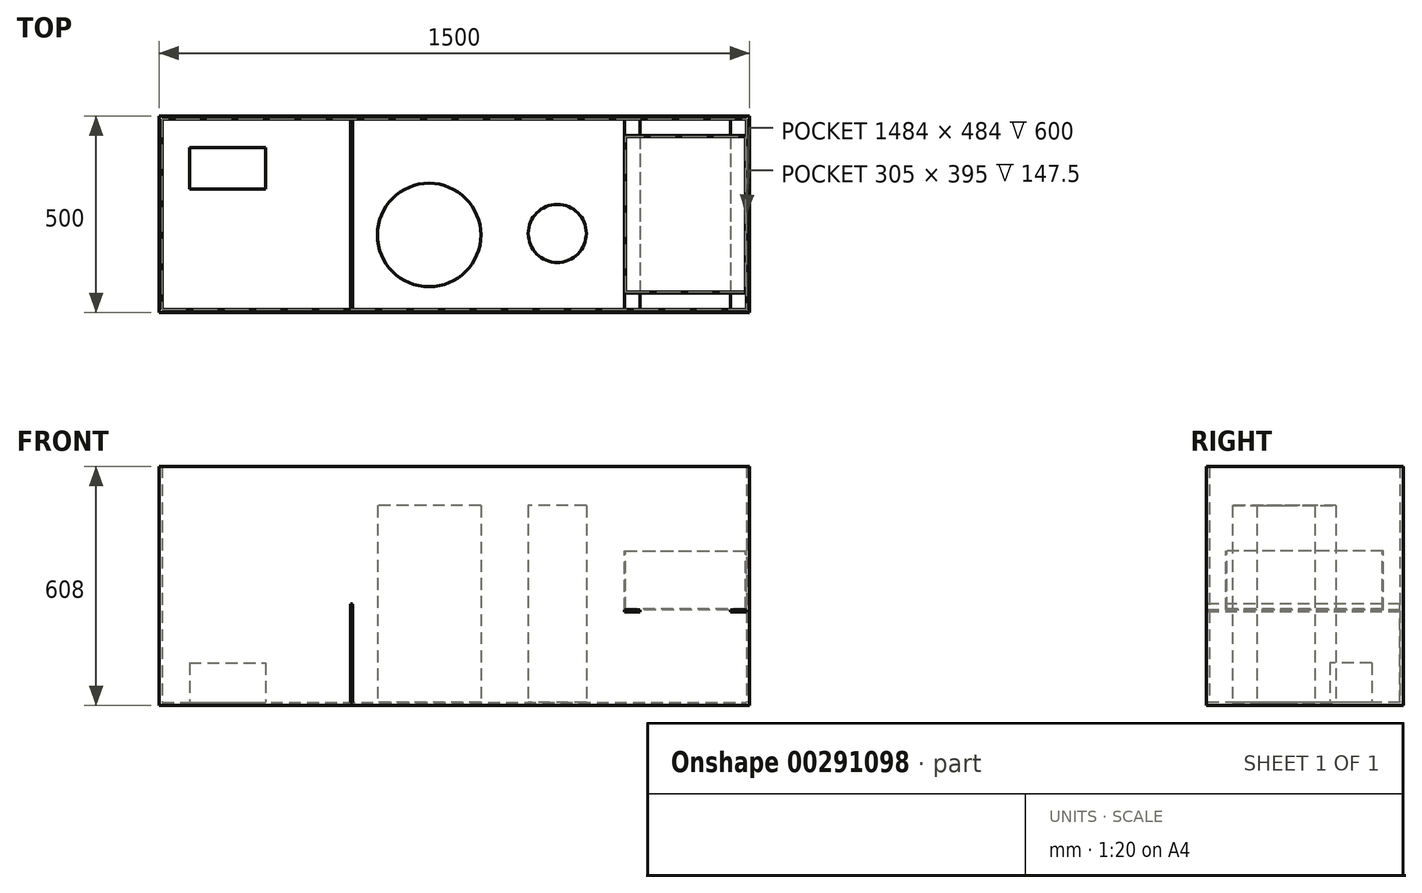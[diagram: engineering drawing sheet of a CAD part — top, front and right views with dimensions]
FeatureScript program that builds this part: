
annotation { "Feature Type Name" : "Feature", "Feature Type Description" : "" }
export const myFeature = defineFeature(function(context is Context, id is Id, definition is map)
    precondition{}
    {
        {
            var Q0;
            Q0=qCreatedBy(makeId("Top.planeOp"),FACE);
            var sketch = newSketch(context, id + "F0", { "sketchPlane" : qUnion([Q0])});
            skLineSegment(sketch, "E0.bottom", {"start": v(-750, 250) * mm, "end": v(750, 250) * mm});
            skLineSegment(sketch, "E0.top", {"start": v(-750, -250) * mm, "end": v(750, -250) * mm});
            skLineSegment(sketch, "E0.left", {"start": v(-750, 250) * mm, "end": v(-750, -250) * mm});
            skLineSegment(sketch, "E0.right", {"start": v(750, 250) * mm, "end": v(750, -250) * mm});
            skPoint(sketch, "E0.middle", {"position": v(0, 0) * mm});
            skLineSegment(sketch, "E1.bottom", {"start": v(-742, 242) * mm, "end": v(742, 242) * mm});
            skLineSegment(sketch, "E1.top", {"start": v(-742, -242) * mm, "end": v(742, -242) * mm});
            skLineSegment(sketch, "E1.left", {"start": v(-742, 242) * mm, "end": v(-742, -242) * mm});
            skLineSegment(sketch, "E1.right", {"start": v(742, 242) * mm, "end": v(742, -242) * mm});
            skSolve(sketch);
        }
        {
            var Q0;
            Q0=qSketchRegion(id+"F0",true);
            var Q1;
            Q1=makeQuery(id+"F0.imprint","IMPRINT",FACE,{"disambiguationData":[TD([[makeQuery(id+"F0.imprint","IMPRINT",EDGE,{"derivedFrom":sQuery(id+"F0.wireOp",EDGE,"E1.bottom")}),-1.0]])]});
            extrude(context, id + "F1", {"entities" : qUnion([Q0, Q1]), "oppositeDirection" : true, "depth" : 8 * mm});
        }
        {
            var Q0;
            Q0=qSketchRegion(id+"F0",true);
            extrude(context, id + "F2", {"entities" : qUnion([Q0]), "depth" : 600 * mm});
        }
        {
            var Q0;
            Q0=makeQuery(id+"F1.opExtrude","SWEPT_BODY",BODY,{"disambiguationData":[OSD([sQuery(id+"F0.wireOp",EDGE,"E0.bottom"),sQuery(id+"F0.wireOp",EDGE,"E0.top"),sQuery(id+"F0.wireOp",EDGE,"E0.left"),sQuery(id+"F0.wireOp",EDGE,"E0.right")])]});
            var Q1;
            Q1=makeQuery(id+"F2.opExtrude","SWEPT_BODY",BODY,{"disambiguationData":[OSD([sQuery(id+"F0.wireOp",EDGE,"E0.bottom"),sQuery(id+"F0.wireOp",EDGE,"E0.top"),sQuery(id+"F0.wireOp",EDGE,"E0.left"),sQuery(id+"F0.wireOp",EDGE,"E0.right"),sQuery(id+"F0.wireOp",EDGE,"E1.bottom"),sQuery(id+"F0.wireOp",EDGE,"E1.top"),sQuery(id+"F0.wireOp",EDGE,"E1.left"),sQuery(id+"F0.wireOp",EDGE,"E1.right")])]});
            booleanBodies(context, id + "F3", {"operationType" : BooleanOperationType.UNION, "tools" : qUnion([Q0, Q1])});
        }
        {
            var Q0;
            {var subQ0=sQuery(id+"F0.wireOp",EDGE,"E0.top");Q0=makeQuery(id+"F3.opBoolean","MERGE",FACE,{"derivedFrom":[makeQuery(id+"F1.opExtrude","SWEPT_FACE",FACE,{"disambiguationData":[OSD([subQ0])]}),makeQuery(id+"F2.opExtrude","SWEPT_FACE",FACE,{"disambiguationData":[OSD([subQ0])]})]});}
            var sketch = newSketch(context, id + "F4", { "sketchPlane" : qUnion([Q0])});
            skLineSegment(sketch, "E2", {"start": v(0, 0) * mm, "end": v(0, 341.46) * mm, "construction": true});
            skLineSegment(sketch, "E3.bottom", {"start": v(-258, 0) * mm, "end": v(-263, 0) * mm});
            skLineSegment(sketch, "E3.top", {"start": v(-258, 250) * mm, "end": v(-263, 250) * mm});
            skLineSegment(sketch, "E3.left", {"start": v(-258, 0) * mm, "end": v(-258, 250) * mm});
            skLineSegment(sketch, "E3.right", {"start": v(-263, 0) * mm, "end": v(-263, 250) * mm});
            skLineSegment(sketch, "E4.bottom", {"start": v(742, 230) * mm, "end": v(702, 230) * mm});
            skLineSegment(sketch, "E4.top", {"start": v(742, 235) * mm, "end": v(702, 235) * mm});
            skLineSegment(sketch, "E4.left", {"start": v(742, 230) * mm, "end": v(742, 235) * mm});
            skLineSegment(sketch, "E4.right", {"start": v(432, 230) * mm, "end": v(432, 235) * mm});
            skLineSegment(sketch, "E5", {"start": v(472, 235) * mm, "end": v(472, 230) * mm});
            skLineSegment(sketch, "E6", {"start": v(702, 235) * mm, "end": v(702, 230) * mm});
            skLineSegment(sketch, "E7", {"start": v(742, 235) * mm, "end": v(742, 214.93) * mm, "construction": true});
            skLineSegment(sketch, "E8.trimOffspring", {"start": v(472, 235) * mm, "end": v(432, 235) * mm});
            skLineSegment(sketch, "E9.trimOffspring", {"start": v(472, 230) * mm, "end": v(432, 230) * mm});
            skSolve(sketch);
        }
        {
            var Q0;
            Q0=qSketchRegion(id+"F4",true);
            var Q1;
            Q1=makeQuery(id+"F2.opExtrude","SWEPT_FACE",FACE,{"disambiguationData":[OSD([sQuery(id+"F0.wireOp",EDGE,"E1.bottom")])]});
            extrude(context, id + "F5", {"entities" : qUnion([Q0]), "endBound" : BoundingType.UP_TO_SURFACE, "oppositeDirection" : true, "endBoundEntityFace" : qUnion([Q1]), "depth" : 25 * mm});
        }
        {
            var Q0;
            Q0=qCreatedBy(makeId("Front.planeOp"),FACE);
            var sketch = newSketch(context, id + "F6", { "sketchPlane" : qUnion([Q0])});
            skLineSegment(sketch, "E10.0", {"start": v(472, 235) * mm, "end": v(432, 235) * mm});
            skLineSegment(sketch, "E11.0", {"start": v(742, 235) * mm, "end": v(702, 235) * mm});
            skLineSegment(sketch, "E12.bottom", {"start": v(432, 235) * mm, "end": v(742, 235) * mm});
            skLineSegment(sketch, "E12.top", {"start": v(432, 385) * mm, "end": v(742, 385) * mm});
            skLineSegment(sketch, "E12.left", {"start": v(432, 235) * mm, "end": v(432, 385) * mm});
            skLineSegment(sketch, "E12.right", {"start": v(742, 235) * mm, "end": v(742, 385) * mm});
            skSolve(sketch);
        }
        {
            var Q0;
            Q0 = qSketchRegion(id + "F6", true);
            extrude(context, id + "F7", {"entities" : qUnion([Q0]), "oppositeDirection" : true, "depth" : 200 * mm, "hasSecondDirection" : true, "secondDirectionOppositeDirection" : false, "secondDirectionDepth" : 200 * mm});
        }
        {
            var Q0;
            Q0=makeQuery(id+"F7.opExtrude","SWEPT_FACE",FACE,{"disambiguationData":[OSD([sQuery(id+"F6.wireOp",EDGE,"E12.top")])]});
            shell(context, id + "F8", {"entities" : qUnion([Q0]), "thickness" : 2.5 * mm});
        }
        {
            var Q0;
            Q0=makeQuery(id+"F1.opExtrude","CAP_FACE",FACE,{"disambiguationData":[OSD([sQuery(id+"F0.wireOp",EDGE,"E0.bottom"),sQuery(id+"F0.wireOp",EDGE,"E0.top"),sQuery(id+"F0.wireOp",EDGE,"E0.left"),sQuery(id+"F0.wireOp",EDGE,"E0.right")])],"isStart":true});
            var sketch = newSketch(context, id + "F9", { "sketchPlane" : qUnion([Q0])});
            skCircle(sketch, "E13", {"center": v(-64.04, -52.45) * mm, "radius": 131.48 * mm});
            skCircle(sketch, "E14", {"center": v(261.6, -48.37) * mm, "radius": 73.85 * mm});
            skSolve(sketch);
        }
        {
            var Q0;
            Q0 = qSketchRegion(id + "F9", true);
            extrude(context, id + "F10", {"entities" : qUnion([Q0]), "depth" : 500 * mm});
        }
        {
            var Q0;
            Q0=makeQuery(id+"F1.opExtrude","CAP_FACE",FACE,{"disambiguationData":[OSD([sQuery(id+"F0.wireOp",EDGE,"E0.bottom"),sQuery(id+"F0.wireOp",EDGE,"E0.top"),sQuery(id+"F0.wireOp",EDGE,"E0.left"),sQuery(id+"F0.wireOp",EDGE,"E0.right")])],"isStart":true});
            var sketch = newSketch(context, id + "F11", { "sketchPlane" : qUnion([Q0])});
            skLineSegment(sketch, "E15.bottom", {"start": v(-673.05, 170) * mm, "end": v(-479.58, 170) * mm});
            skLineSegment(sketch, "E15.top", {"start": v(-673.05, 63.71) * mm, "end": v(-479.58, 63.71) * mm});
            skLineSegment(sketch, "E15.left", {"start": v(-673.05, 170) * mm, "end": v(-673.05, 63.71) * mm});
            skLineSegment(sketch, "E15.right", {"start": v(-479.58, 170) * mm, "end": v(-479.58, 63.71) * mm});
            skSolve(sketch);
        }
        {
            var Q0;
            Q0 = qSketchRegion(id + "F11", true);
            extrude(context, id + "F12", {"entities" : qUnion([Q0]), "depth" : 100 * mm});
        }
    });
